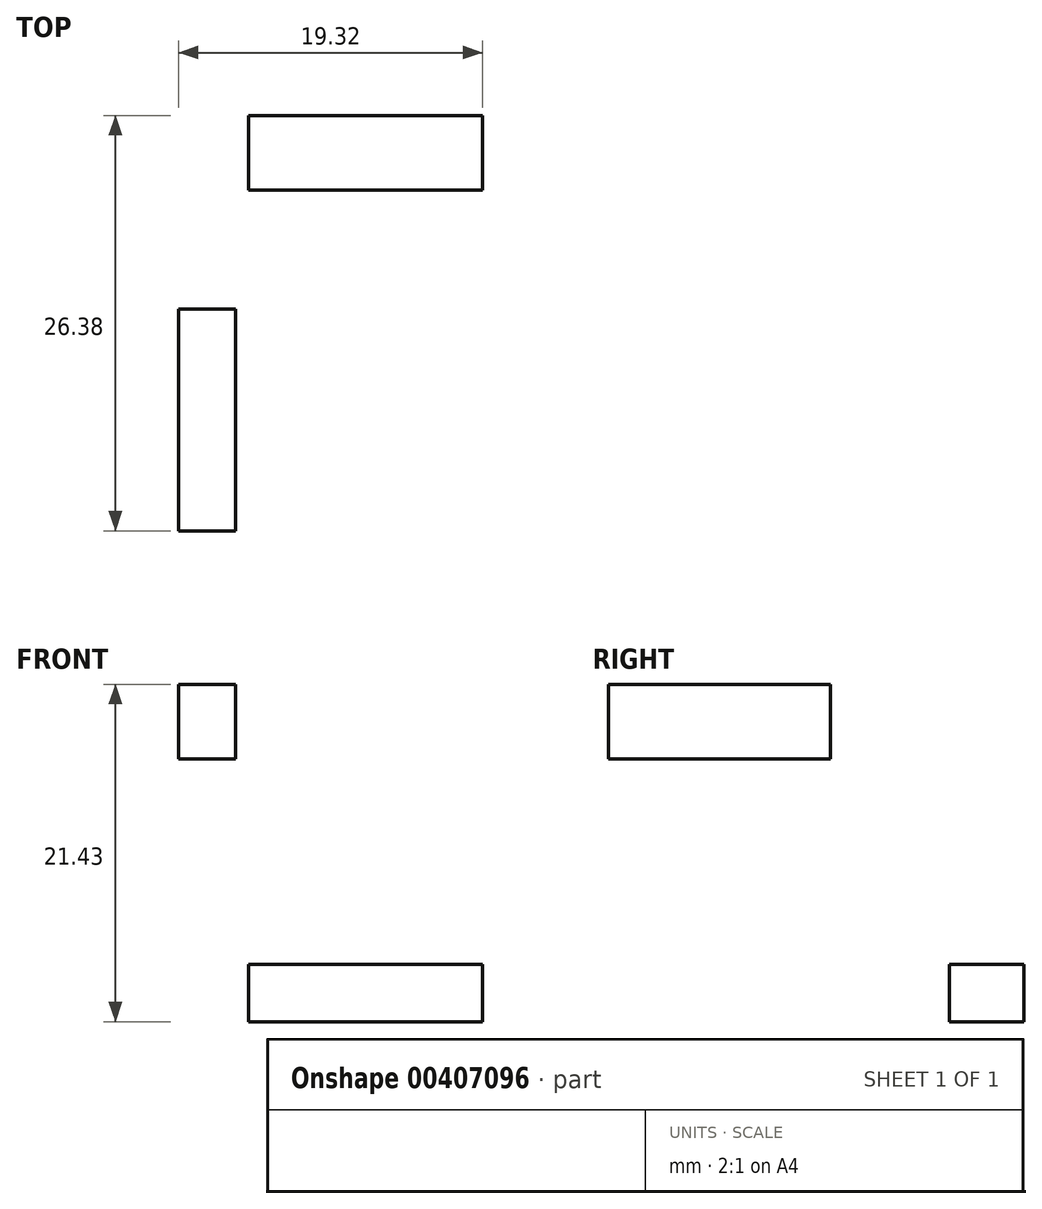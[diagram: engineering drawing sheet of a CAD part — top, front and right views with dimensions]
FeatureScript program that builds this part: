
annotation { "Feature Type Name" : "Feature", "Feature Type Description" : "" }
export const myFeature = defineFeature(function(context is Context, id is Id, definition is map)
    precondition{}
    {
        {
            var Q0;
            Q0=qCreatedBy(makeId("Front.planeOp"),FACE);
            var sketch = newSketch(context, id + "F0", { "sketchPlane" : qUnion([Q0])});
            skLineSegment(sketch, "E0", {"start": v(0, 0) * mm, "end": v(14.27, 0) * mm});
            skLineSegment(sketch, "E1", {"start": v(0, 0) * mm, "end": v(0, 8.06) * mm});
            skLineSegment(sketch, "E2", {"start": v(0, 8.06) * mm, "end": v(14.4, 8.06) * mm});
            skLineSegment(sketch, "E3", {"start": v(14.4, 8.06) * mm, "end": v(14.27, 0) * mm});
            skLineSegment(sketch, "E4.bottom", {"start": v(-33.8, 21.43) * mm, "end": v(-30.16, 21.43) * mm});
            skLineSegment(sketch, "E4.top", {"start": v(-35.2, 16.7) * mm, "end": v(-30.16, 16.7) * mm});
            skLineSegment(sketch, "E4.left", {"start": v(-33.8, 21.43) * mm, "end": v(-33.8, 16.7) * mm});
            skLineSegment(sketch, "E4.right", {"start": v(-30.16, 21.43) * mm, "end": v(-30.16, 16.7) * mm});
            skSolve(sketch);
        }
        {
            var Q0;
            Q0=makeQuery(id+"F0.imprint","IMPRINT",FACE,{"disambiguationData":[TD([[makeQuery(id+"F0.imprint","IMPRINT",EDGE,{"derivedFrom":sQuery(id+"F0.wireOp",EDGE,"E4.bottom")}),-1.0]])]});
            extrude(context, id + "F1", {"entities" : qUnion([Q0]), "depth" : 14.08 * mm});
        }
        {
            var Q0;
            Q0=qCreatedBy(makeId("Top.planeOp"),FACE);
            var sketch = newSketch(context, id + "F2", { "sketchPlane" : qUnion([Q0])});
            skLineSegment(sketch, "E5.bottom", {"start": v(-29.35, 12.3) * mm, "end": v(-14.5, 12.3) * mm});
            skLineSegment(sketch, "E5.top", {"start": v(-29.35, 7.56) * mm, "end": v(-14.5, 7.56) * mm});
            skLineSegment(sketch, "E5.left", {"start": v(-29.35, 12.3) * mm, "end": v(-29.35, 7.56) * mm});
            skLineSegment(sketch, "E5.right", {"start": v(-14.5, 12.3) * mm, "end": v(-14.5, 7.56) * mm});
            skSolve(sketch);
        }
        {
            var Q0;
            Q0=makeQuery(id+"F2.imprint","IMPRINT",FACE,{"disambiguationData":[TD([[makeQuery(id+"F2.imprint","IMPRINT",EDGE,{"derivedFrom":sQuery(id+"F2.wireOp",EDGE,"E5.bottom")}),-1.0]])]});
            extrude(context, id + "F3", {"entities" : qUnion([Q0]), "depth" : 3.64 * mm, "offsetDistance" : 25.4 * mm});
        }
    });
